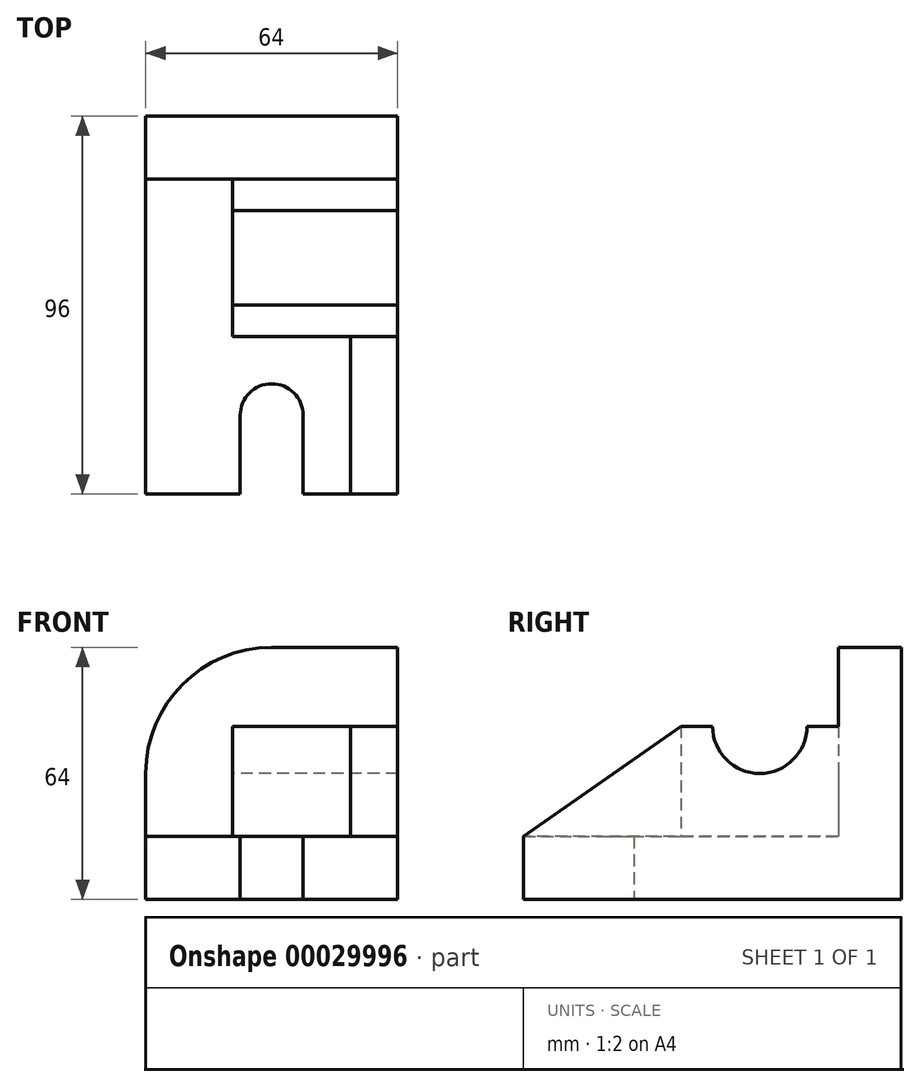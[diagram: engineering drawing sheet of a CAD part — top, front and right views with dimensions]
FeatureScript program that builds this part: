
annotation { "Feature Type Name" : "Feature", "Feature Type Description" : "" }
export const myFeature = defineFeature(function(context is Context, id is Id, definition is map)
    precondition{}
    {
        {
            var Q0;
            Q0=qCreatedBy(makeId("Top.planeOp"),FACE);
            var sketch = newSketch(context, id + "F0", { "sketchPlane" : qUnion([Q0])});
            skLineSegment(sketch, "E0.rect.bottom", {"start": v(-32, 48) * mm, "end": v(32, 48) * mm});
            skLineSegment(sketch, "E0.rect.top", {"start": v(-32, -48) * mm, "end": v(-8, -48) * mm});
            skLineSegment(sketch, "E0.rect.left", {"start": v(-32, 48) * mm, "end": v(-32, -48) * mm});
            skLineSegment(sketch, "E0.rect.right", {"start": v(32, 48) * mm, "end": v(32, -48) * mm});
            skPoint(sketch, "E0.rect.middle", {"position": v(0, 0) * mm});
            skLineSegment(sketch, "E1", {"start": v(46.76, 48) * mm, "end": v(46.76, 32) * mm});
            skLineSegment(sketch, "E2", {"start": v(32, 48) * mm, "end": v(32, 32) * mm});
            skLineSegment(sketch, "E3", {"start": v(32, 32) * mm, "end": v(-32, 32) * mm});
            skLineSegment(sketch, "E4", {"start": v(-32, 32) * mm, "end": v(-32, 48) * mm});
            skLineSegment(sketch, "E5", {"start": v(32, -60.53) * mm, "end": v(20, -60.53) * mm});
            skLineSegment(sketch, "E6", {"start": v(32, -48) * mm, "end": v(20, -48) * mm});
            skLineSegment(sketch, "E7", {"start": v(20, -48) * mm, "end": v(20, -8) * mm});
            skLineSegment(sketch, "E8", {"start": v(20, -8) * mm, "end": v(32, -8) * mm});
            skLineSegment(sketch, "E9", {"start": v(32, -8) * mm, "end": v(32, -48) * mm});
            skLineSegment(sketch, "E10", {"start": v(0, -61.5) * mm, "end": v(-8, -61.5) * mm});
            skLineSegment(sketch, "E11", {"start": v(-8, -48) * mm, "end": v(-8, -28) * mm});
            skLineSegment(sketch, "E12.MirrorCS", {"start": v(8, -48) * mm, "end": v(8, -28) * mm});
            skArc(sketch, "E13", {"start": v(8, -28) * mm, "mid": v(0, -20) * mm, "end": v(-8, -28) * mm});
            skLineSegment(sketch, "E14.trimOffspring", {"start": v(8, -48) * mm, "end": v(32, -48) * mm});
            skPoint(sketch, "E15.MirrorCS.end.orphan", {"position": v(8, -48) * mm});
            skPoint(sketch, "E16.start.orphan", {"position": v(0, -48) * mm});
            skSolve(sketch);
        }
        {
            var Q0;
            {var subQ2=sQuery(id+"F0.wireOp",EDGE,"E7");Q0=makeQuery(id+"F0.imprint","IMPRINT",FACE,{"disambiguationData":[TD([[makeQuery(id+"F0.imprint","IMPRINT",EDGE,{"derivedFrom":subQ2}),-1.0]])]});}
            extrude(context, id + "F1", {"entities" : qUnion([Q0]), "depth" : 44 * mm});
        }
        {
            var Q0;
            Q0 = qSketchRegion(id + "F0", true);
            extrude(context, id + "F2", {"entities" : qUnion([Q0]), "operationType" : NewBodyOperationType.ADD, "depth" : 16 * mm});
        }
        {
            var Q0;
            Q0=makeQuery(id+"F0.imprint","IMPRINT",FACE,{"disambiguationData":[TD([[makeQuery(id+"F0.imprint","IMPRINT",EDGE,{"derivedFrom":sQuery(id+"F0.wireOp",EDGE,"E0.rect.bottom")}),-1.0]])]});
            extrude(context, id + "F3", {"entities" : qUnion([Q0]), "operationType" : NewBodyOperationType.ADD, "depth" : 64 * mm});
        }
        {
            var Q0;
            Q0=makeQuery(id+"F2.opExtrude","CAP_FACE",FACE,{"disambiguationData":[OSD([sQuery(id+"F0.wireOp",EDGE,"E0.rect.bottom"),sQuery(id+"F0.wireOp",EDGE,"E0.rect.top"),sQuery(id+"F0.wireOp",EDGE,"E0.rect.left"),sQuery(id+"F0.wireOp",EDGE,"E0.rect.right"),sQuery(id+"F0.wireOp",EDGE,"E2"),sQuery(id+"F0.wireOp",EDGE,"E4"),sQuery(id+"F0.wireOp",EDGE,"E9"),sQuery(id+"F0.wireOp",EDGE,"E11"),sQuery(id+"F0.wireOp",EDGE,"E12.MirrorCS"),sQuery(id+"F0.wireOp",EDGE,"E13"),sQuery(id+"F0.wireOp",EDGE,"E14.trimOffspring")])],"isStart":false});
            var sketch = newSketch(context, id + "F4", { "sketchPlane" : qUnion([Q0])});
            skLineSegment(sketch, "E17", {"start": v(-32, -66.94) * mm, "end": v(-10, -66.94) * mm});
            skLineSegment(sketch, "E18", {"start": v(-10, 32) * mm, "end": v(32, 32) * mm});
            skLineSegment(sketch, "E19", {"start": v(32, 32) * mm, "end": v(32, -8) * mm});
            skLineSegment(sketch, "E20", {"start": v(32, -8) * mm, "end": v(-10, -8) * mm});
            skLineSegment(sketch, "E21", {"start": v(-10, -8) * mm, "end": v(-10, 32) * mm});
            skSolve(sketch);
        }
        {
            var Q0;
            Q0 = qSketchRegion(id + "F4", true);
            extrude(context, id + "F5", {"entities" : qUnion([Q0]), "operationType" : NewBodyOperationType.ADD, "depth" : 28 * mm});
        }
        {
            var Q0;
            Q0=makeQuery(id+"F1.opExtrude","SWEPT_FACE",FACE,{"disambiguationData":[OSD([sQuery(id+"F0.wireOp",EDGE,"E7")])]});
            var sketch = newSketch(context, id + "F6", { "sketchPlane" : qUnion([Q0])});
            skLineSegment(sketch, "E22", {"start": v(48, 16) * mm, "end": v(8, 44) * mm});
            skLineSegment(sketch, "E23", {"start": v(8, 44) * mm, "end": v(48, 44) * mm});
            skLineSegment(sketch, "E24", {"start": v(48, 44) * mm, "end": v(48, 16) * mm});
            skSolve(sketch);
        }
        {
            var Q0;
            Q0 = qSketchRegion(id + "F6", true);
            extrude(context, id + "F7", {"entities" : qUnion([Q0]), "operationType" : NewBodyOperationType.REMOVE, "endBound" : BoundingType.THROUGH_ALL, "oppositeDirection" : true, "depth" : 25 * mm});
        }
        {
            var Q0;
            Q0=makeQuery(id+"F5.opExtrude","SWEPT_FACE",FACE,{"disambiguationData":[OSD([sQuery(id+"F4.wireOp",EDGE,"E21")])]});
            var sketch = newSketch(context, id + "F8", { "sketchPlane" : qUnion([Q0])});
            skArc(sketch, "E25", {"start": v(-24, 44) * mm, "mid": v(-12, 32) * mm, "end": v(0, 44) * mm});
            skPoint(sketch, "E26.start.orphan", {"position": v(8, 56.33) * mm});
            skLineSegment(sketch, "E27", {"start": v(-24, 44) * mm, "end": v(0, 44) * mm});
            skSolve(sketch);
        }
        {
            var Q0;
            Q0 = qSketchRegion(id + "F8", true);
            extrude(context, id + "F9", {"entities" : qUnion([Q0]), "operationType" : NewBodyOperationType.REMOVE, "endBound" : BoundingType.THROUGH_ALL, "oppositeDirection" : true, "depth" : 25 * mm});
        }
        {
            var Q0;
            {var subQ0=sQuery(id+"F0.wireOp",EDGE,"E0.rect.bottom");Q0=makeQuery(id+"F3.boolean.opBoolean","MERGE",FACE,{"derivedFrom":[makeQuery(id+"F2.opExtrude","SWEPT_FACE",FACE,{"disambiguationData":[OSD([subQ0])]}),makeQuery(id+"F3.opExtrude","SWEPT_FACE",FACE,{"disambiguationData":[OSD([subQ0])]})]});}
            var sketch = newSketch(context, id + "F10", { "sketchPlane" : qUnion([Q0])});
            skArc(sketch, "E28", {"start": v(32, 32) * mm, "mid": v(22.63, 54.63) * mm, "end": v(0, 64) * mm});
            skPoint(sketch, "E29.orphan", {"position": v(0, 0) * mm});
            skLineSegment(sketch, "E30", {"start": v(0, 64) * mm, "end": v(32, 64) * mm});
            skLineSegment(sketch, "E31", {"start": v(32, 64) * mm, "end": v(32, 32) * mm});
            skSolve(sketch);
        }
        {
            var Q0;
            Q0 = qSketchRegion(id + "F10", true);
            extrude(context, id + "F11", {"entities" : qUnion([Q0]), "operationType" : NewBodyOperationType.REMOVE, "endBound" : BoundingType.THROUGH_ALL, "oppositeDirection" : true, "depth" : 25 * mm});
        }
    });
